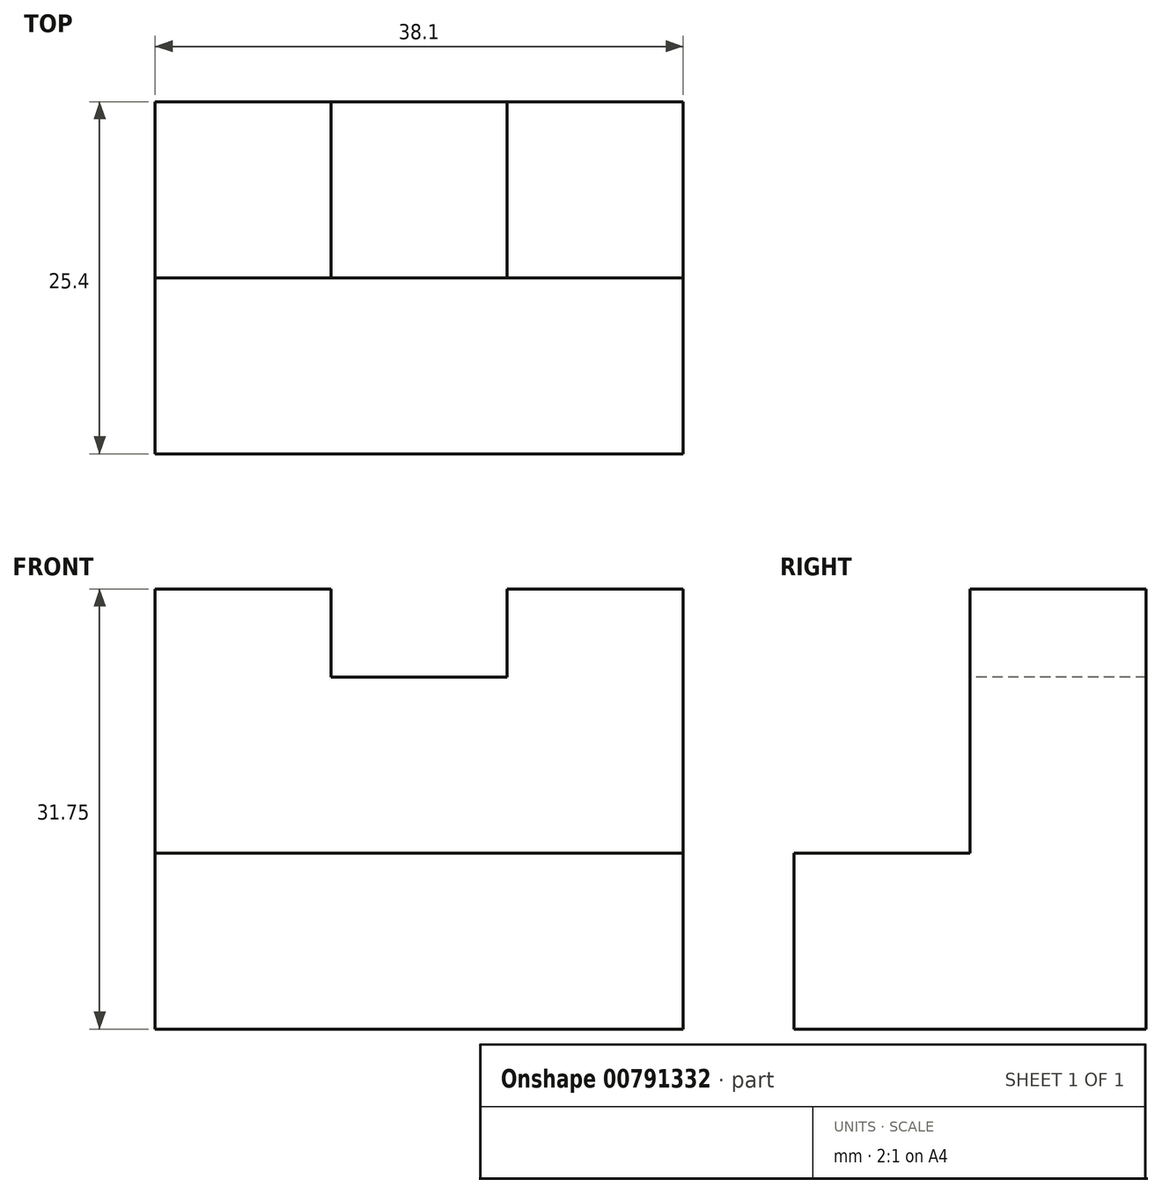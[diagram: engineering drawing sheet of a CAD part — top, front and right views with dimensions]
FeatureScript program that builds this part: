
annotation { "Feature Type Name" : "Feature", "Feature Type Description" : "" }
export const myFeature = defineFeature(function(context is Context, id is Id, definition is map)
    precondition{}
    {
        {
            var Q0;
            Q0=qCreatedBy(makeId("Right.planeOp"),FACE);
            var sketch = newSketch(context, id + "F0", { "sketchPlane" : qUnion([Q0])});
            skLineSegment(sketch, "E0", {"start": v(0, 0) * mm, "end": v(25.4, 0) * mm});
            skLineSegment(sketch, "E1", {"start": v(25.4, 0) * mm, "end": v(25.4, 31.75) * mm});
            skLineSegment(sketch, "E2", {"start": v(25.4, 31.75) * mm, "end": v(0, 31.75) * mm});
            skLineSegment(sketch, "E3", {"start": v(0, 31.75) * mm, "end": v(0, 0) * mm});
            skSolve(sketch);
        }
        {
            var Q0;
            Q0 = qSketchRegion(id + "F0", true);
            extrude(context, id + "F1", {"entities" : qUnion([Q0]), "depth" : 38.1 * mm, "offsetDistance" : 25.4 * mm});
        }
        {
            var Q0;
            Q0=makeQuery(id+"F1.opExtrude","CAP_FACE",FACE,{"disambiguationData":[OSD([sQuery(id+"F0.wireOp",EDGE,"E0"),sQuery(id+"F0.wireOp",EDGE,"E1"),sQuery(id+"F0.wireOp",EDGE,"E2"),sQuery(id+"F0.wireOp",EDGE,"E3")])],"isStart":false});
            var sketch = newSketch(context, id + "F2", { "sketchPlane" : qUnion([Q0])});
            skLineSegment(sketch, "E4", {"start": v(0, 0) * mm, "end": v(0, 12.7) * mm, "construction": true});
            skLineSegment(sketch, "E5", {"start": v(0, 12.7) * mm, "end": v(12.7, 12.7) * mm});
            skLineSegment(sketch, "E6", {"start": v(12.7, 12.7) * mm, "end": v(12.7, 31.75) * mm});
            skSolve(sketch);
        }
        {
            var Q0;
            Q0 = qSketchRegion(id + "F2", true);
            var Q1;
            {var subQ0=sQuery(id+"F2.wireOp",EDGE,"E5");Q1=makeQuery(id+"F2.imprint","IMPRINT",FACE,{"disambiguationData":[TD([[makeQuery(id+"F2.imprint","IMPRINT",EDGE,{"derivedFrom":subQ0}),1.0]])]});}
            extrude(context, id + "F3", {"entities" : qUnion([Q0, Q1]), "operationType" : NewBodyOperationType.REMOVE, "oppositeDirection" : true, "depth" : 50.8 * mm, "offsetDistance" : 25.4 * mm});
        }
        {
            var Q0;
            Q0=makeQuery(id+"F3.boolean.opBoolean","COPY",FACE,{"derivedFrom":makeQuery(id+"F3.opExtrude","SWEPT_FACE",FACE,{"disambiguationData":[OSD([sQuery(id+"F2.wireOp",EDGE,"E6")])]})});
            var sketch = newSketch(context, id + "F4", { "sketchPlane" : qUnion([Q0])});
            skLineSegment(sketch, "E7", {"start": v(0, 31.75) * mm, "end": v(12.7, 31.75) * mm, "construction": true});
            skLineSegment(sketch, "E8", {"start": v(12.7, 31.75) * mm, "end": v(12.7, 25.4) * mm});
            skLineSegment(sketch, "E9", {"start": v(12.7, 25.4) * mm, "end": v(25.4, 25.4) * mm});
            skLineSegment(sketch, "E10", {"start": v(25.4, 25.4) * mm, "end": v(25.4, 31.75) * mm});
            skSolve(sketch);
        }
        {
            var Q0;
            {var subQ0=sQuery(id+"F4.wireOp",EDGE,"E8");Q0=makeQuery(id+"F4.imprint","IMPRINT",FACE,{"disambiguationData":[TD([[makeQuery(id+"F4.imprint","IMPRINT",EDGE,{"derivedFrom":subQ0}),1.0]])]});}
            extrude(context, id + "F5", {"entities" : qUnion([Q0]), "operationType" : NewBodyOperationType.REMOVE, "oppositeDirection" : true, "depth" : 25.4 * mm, "offsetDistance" : 25.4 * mm});
        }
    });
